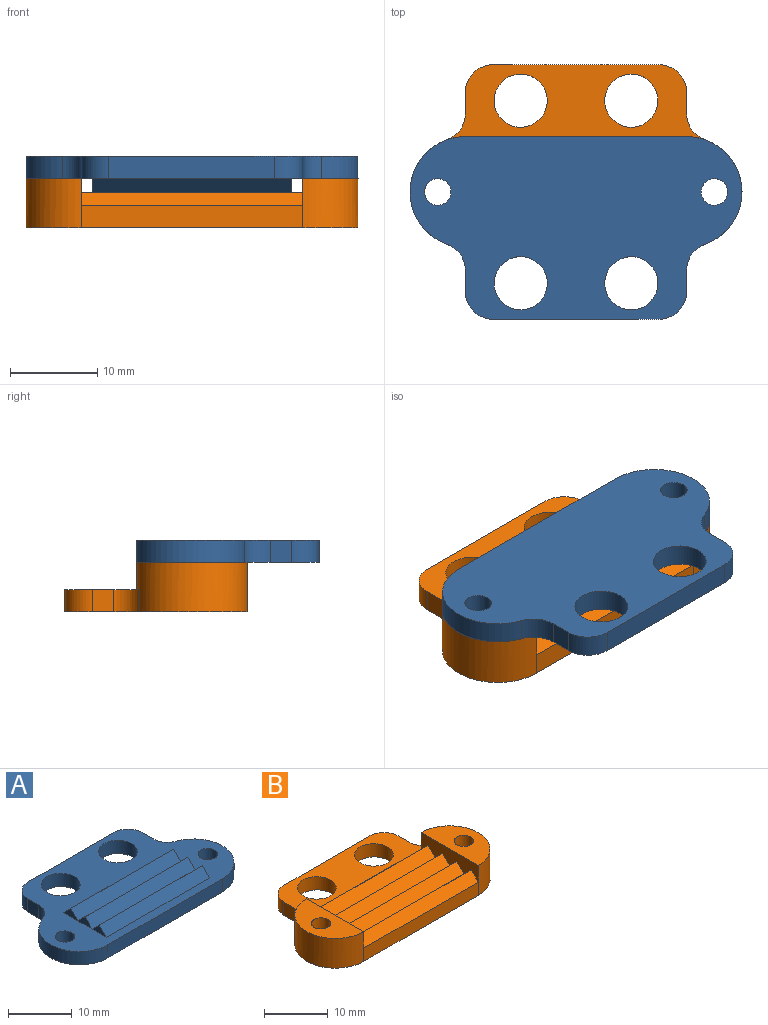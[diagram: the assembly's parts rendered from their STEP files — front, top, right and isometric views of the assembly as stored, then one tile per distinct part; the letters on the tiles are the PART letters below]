
ASSEMBLY  parts=2 mates=1
PART A: 28 faces, bbox 38.1x21x4.1 mm
  f0: plane 38.1x20.96mm, normal (0,0,1), area 366.3mm2, adj f1,f2,f3,f6,f7,f8,f11,f12
  f1: plane 25.4x2.54mm, normal (0,-1,0), area 64.5mm2, adj f0,f4,f17,f18
  f2: cylinder r=1.52mm len=3.05mm, axis (0,0,-1), area 24.3mm2, adj f0,f4
  f3: cylinder r=1.52mm len=3.05mm, axis (0,0,-1), area 24.3mm2, adj f0,f4
  f4: plane 38.1x20.96mm, normal (0,0,-1), area 584mm2, adj f1,f2,f3,f17,f18,f19,f20,f21
  f5: plane 22.86x1.59mm, normal (0,-0.71,0.71), area 51.3mm2, adj f6,f7,f8,f10
  f6: plane 22.86x1.59mm, normal (0,0.71,0.71), area 51.3mm2, adj f0,f5,f7,f8
  f7: plane 3.18x1.59mm, normal (1,0,0), area 2.5mm2, adj f0,f5,f6
  f8: plane 3.18x1.59mm, normal (-1,0,0), area 2.5mm2, adj f0,f5,f6
  f9: plane 22.86x1.59mm, normal (0,-0.71,0.71), area 51.3mm2, adj f10,f11,f12,f13
  f10: plane 22.86x1.59mm, normal (0,0.71,0.71), area 51.3mm2, adj f5,f9,f11,f12
  f11: plane 3.18x1.59mm, normal (1,0,0), area 2.5mm2, adj f0,f9,f10
  f12: plane 3.18x1.59mm, normal (-1,0,0), area 2.5mm2, adj f0,f9,f10
  f13: plane 22.86x1.59mm, normal (0,0.71,0.71), area 51.3mm2, adj f9,f14,f15,f16
  f14: plane 22.86x1.59mm, normal (0,-0.71,0.71), area 51.3mm2, adj f0,f13,f15,f16
  f15: plane 3.18x1.59mm, normal (1,0,0), area 2.5mm2, adj f0,f13,f14
  f16: plane 3.18x1.59mm, normal (-1,0,0), area 2.5mm2, adj f0,f13,f14
  f17: cylinder r=6.35mm len=12.34mm, axis (0,0,-1), area 45.2mm2, adj f0,f1,f4,f26
  f18: cylinder r=6.35mm len=12.34mm, axis (0,0,-1), area 45.2mm2, adj f0,f1,f4,f27
  f19: plane 2.54x2.45mm, normal (-1,0,0), area 6.2mm2, adj f0,f4,f25,f26
  f20: plane 2.54x2.45mm, normal (1,0,0), area 6.2mm2, adj f0,f4,f24,f27
  f21: cylinder r=3.05mm len=6.1mm, axis (0,0,1), area 48.6mm2, adj f0,f4
  f22: plane 19.05x2.54mm, normal (0,1,0), area 48.4mm2, adj f0,f4,f24,f25
  f23: cylinder r=3.05mm len=6.1mm, axis (0,0,1), area 48.6mm2, adj f0,f4
  f24: cylinder r=3.17mm len=3.18mm, axis (0,0,-1), area 12.7mm2, adj f0,f4,f20,f22
  f25: cylinder r=3.17mm len=3.18mm, axis (0,0,1), area 12.7mm2, adj f0,f4,f19,f22
  f26: cylinder r=3.17mm len=2.99mm, axis (0,0,-1), area 9.9mm2, adj f0,f4,f17,f19
  f27: cylinder r=3.17mm len=2.99mm, axis (0,0,-1), area 9.9mm2, adj f0,f4,f18,f20
PART B: 28 faces, bbox 38.1x21x5.7 mm
  f0: plane 12.7x3.18mm, normal (1,0,0), area 30.2mm2, adj f4,f6,f7,f8,f9,f10,f11,f12
  f1: plane 12.7x3.18mm, normal (-1,0,0), area 30.2mm2, adj f5,f6,f7,f8,f9,f10,f11,f12
  f2: plane 25.4x2.54mm, normal (0,-1,0), area 64.5mm2, adj f3,f6,f16,f17
  f3: plane 38.1x20.96mm, normal (0,0,-1), area 584mm2, adj f2,f14,f15,f16,f17,f18,f19,f20
  f4: plane 12.7x6.35mm, normal (0,0,1), area 56mm2, adj f0,f15,f17
  f5: plane 12.7x6.35mm, normal (0,0,1), area 56mm2, adj f1,f14,f16
  f6: plane 25.4x1.59mm, normal (0,-0.71,0.71), area 57mm2, adj f0,f1,f2,f7
  f7: plane 25.4x1.59mm, normal (0,0.71,0.71), area 57mm2, adj f0,f1,f6,f8
  f8: plane 25.4x1.59mm, normal (0,-0.71,0.71), area 57mm2, adj f0,f1,f7,f9
  f9: plane 25.4x1.59mm, normal (0,0.71,0.71), area 57mm2, adj f0,f1,f8,f10
  f10: plane 25.4x1.59mm, normal (0,-0.71,0.71), area 57mm2, adj f0,f1,f9,f11
  f11: plane 25.4x1.59mm, normal (0,0.71,0.71), area 57mm2, adj f0,f1,f10,f13
  f12: plane 25.4x1.59mm, normal (0,0.71,0.71), area 57mm2, adj f0,f1,f13,f23
  f13: plane 25.4x1.59mm, normal (0,-0.71,0.71), area 57mm2, adj f0,f1,f11,f12
  f14: cylinder r=1.52mm len=5.72mm, axis (0,0,1), area 54.7mm2, adj f3,f5
  f15: cylinder r=1.52mm len=5.72mm, axis (0,0,1), area 54.7mm2, adj f3,f4
  f16: cylinder r=6.35mm len=12.7mm, axis (0,0,-1), area 108.5mm2, adj f1,f2,f3,f5,f23,f26
  f17: cylinder r=6.35mm len=12.7mm, axis (0,0,1), area 108.5mm2, adj f0,f2,f3,f4,f23,f27
  f18: plane 2.54x2.45mm, normal (-1,0,0), area 6.2mm2, adj f3,f23,f24,f27
  f19: plane 19.05x2.54mm, normal (0,1,0), area 48.4mm2, adj f3,f23,f24,f25
  f20: cylinder r=3.05mm len=6.1mm, axis (0,0,-1), area 48.6mm2, adj f3,f23
  f21: cylinder r=3.05mm len=6.1mm, axis (0,0,-1), area 48.6mm2, adj f3,f23
  f22: plane 2.54x2.45mm, normal (1,0,0), area 6.2mm2, adj f3,f23,f25,f26
  f23: plane 29.63x8.62mm, normal (0,0,1), area 149.4mm2, adj f12,f16,f17,f18,f19,f20,f21,f22
  f24: cylinder r=3.17mm len=3.18mm, axis (0,0,-1), area 12.7mm2, adj f3,f18,f19,f23
  f25: cylinder r=3.17mm len=3.18mm, axis (0,0,1), area 12.7mm2, adj f3,f19,f22,f23
  f26: cylinder r=3.17mm len=2.99mm, axis (0,0,-1), area 9.9mm2, adj f3,f16,f22,f23
  f27: cylinder r=3.17mm len=2.99mm, axis (0,0,1), area 9.9mm2, adj f3,f17,f18,f23
PLACE A rot(axis=(1,0,0),180deg) t=(0,0,14.1)mm
PLACE B at identity
MATE revolute A.f3 <-> B.f14  axis (0,0,-1) through (15.88,0,5.72)mm
